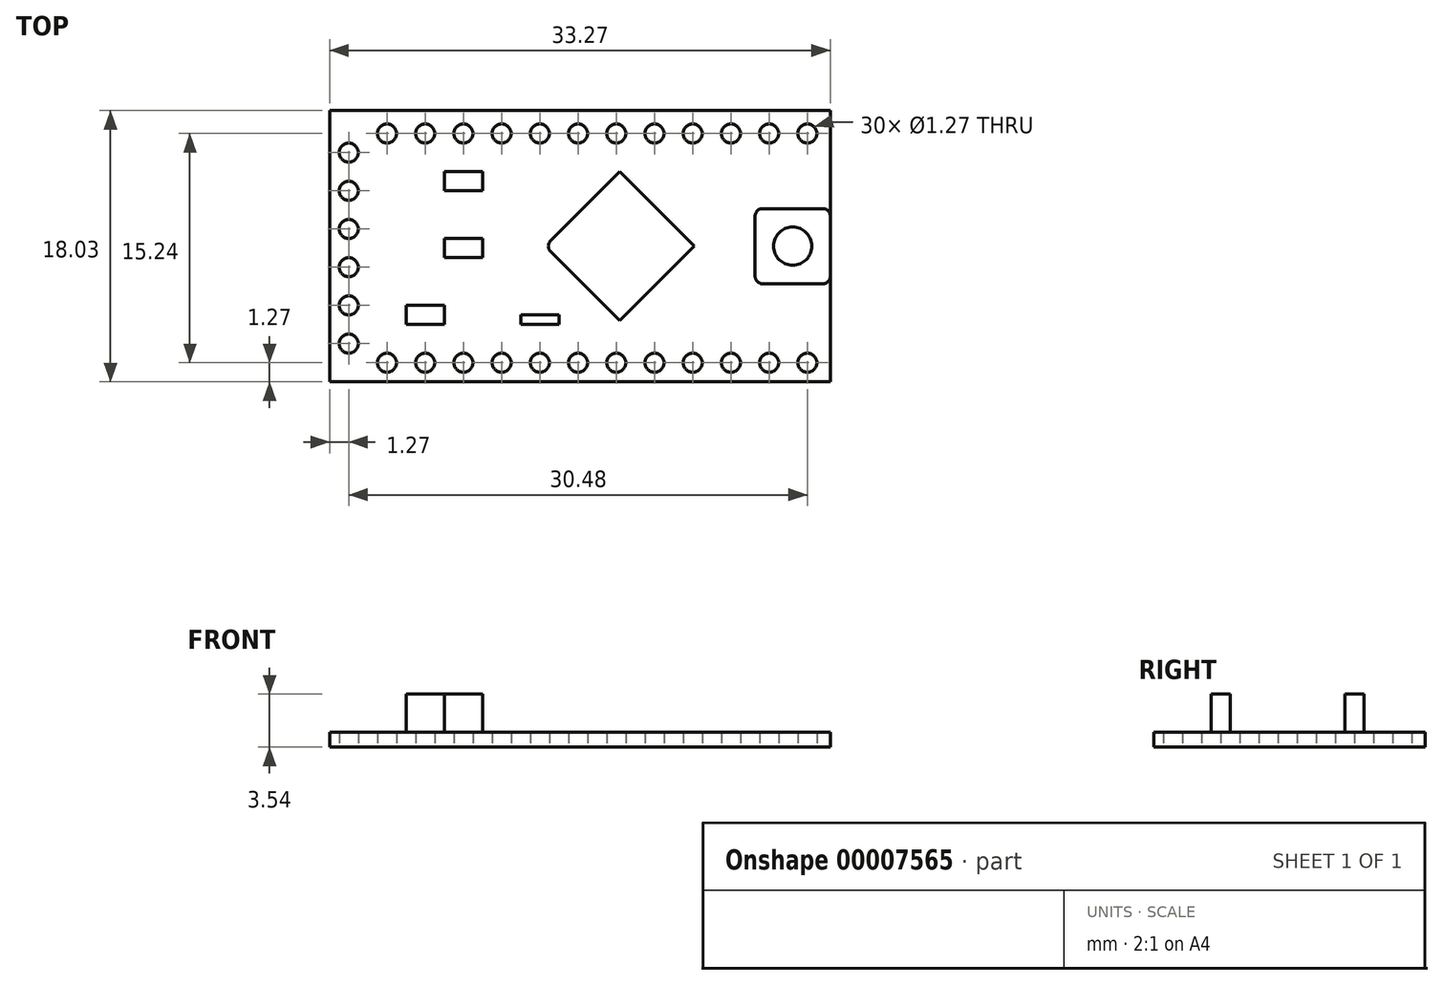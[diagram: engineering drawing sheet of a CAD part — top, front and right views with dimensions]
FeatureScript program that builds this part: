
annotation { "Feature Type Name" : "Feature", "Feature Type Description" : "" }
export const myFeature = defineFeature(function(context is Context, id is Id, definition is map)
    precondition{}
    {
        {
            var Q0;
            Q0=qCreatedBy(makeId("Top.planeOp"),FACE);
            var sketch = newSketch(context, id + "F0", { "sketchPlane" : qUnion([Q0])});
            skLineSegment(sketch, "E0.bottom", {"start": v(0, 0) * mm, "end": v(33.27, 0) * mm});
            skLineSegment(sketch, "E0.top", {"start": v(0, 18.03) * mm, "end": v(33.27, 18.03) * mm});
            skLineSegment(sketch, "E0.left", {"start": v(0, 0) * mm, "end": v(0, 18.03) * mm});
            skLineSegment(sketch, "E0.right", {"start": v(33.27, 0) * mm, "end": v(33.27, 18.03) * mm});
            skCircle(sketch, "E1", {"center": v(31.75, 16.51) * mm, "radius": 0.64 * mm});
            skCircle(sketch, "E2.1.0.0", {"center": v(29.21, 16.51) * mm, "radius": 0.64 * mm});
            skCircle(sketch, "E2.2.0.0", {"center": v(26.67, 16.51) * mm, "radius": 0.64 * mm});
            skCircle(sketch, "E2.3.0.0", {"center": v(24.13, 16.51) * mm, "radius": 0.64 * mm});
            skCircle(sketch, "E2.4.0.0", {"center": v(21.6, 16.51) * mm, "radius": 0.64 * mm});
            skCircle(sketch, "E2.5.0.0", {"center": v(19.05, 16.51) * mm, "radius": 0.64 * mm});
            skCircle(sketch, "E2.6.0.0", {"center": v(16.51, 16.51) * mm, "radius": 0.64 * mm});
            skCircle(sketch, "E2.7.0.0", {"center": v(13.97, 16.51) * mm, "radius": 0.64 * mm});
            skCircle(sketch, "E2.8.0.0", {"center": v(11.43, 16.51) * mm, "radius": 0.64 * mm});
            skCircle(sketch, "E2.9.0.0", {"center": v(8.9, 16.51) * mm, "radius": 0.64 * mm});
            skCircle(sketch, "E2.10.0.0", {"center": v(6.35, 16.51) * mm, "radius": 0.64 * mm});
            skCircle(sketch, "E2.11.0.0", {"center": v(3.8, 16.51) * mm, "radius": 0.64 * mm});
            skLineSegment(sketch, "E2.direction1", {"start": v(31.75, 16.51) * mm, "end": v(29.21, 16.51) * mm, "construction": true});
            skCircle(sketch, "E3.0.1.0", {"center": v(31.75, 1.27) * mm, "radius": 0.64 * mm});
            skCircle(sketch, "E3.0.1.1", {"center": v(26.67, 1.27) * mm, "radius": 0.64 * mm});
            skCircle(sketch, "E3.0.1.2", {"center": v(29.21, 1.27) * mm, "radius": 0.64 * mm});
            skCircle(sketch, "E3.0.1.3", {"center": v(21.6, 1.27) * mm, "radius": 0.64 * mm});
            skCircle(sketch, "E3.0.1.4", {"center": v(24.13, 1.27) * mm, "radius": 0.64 * mm});
            skCircle(sketch, "E3.0.1.5", {"center": v(16.51, 1.27) * mm, "radius": 0.64 * mm});
            skCircle(sketch, "E3.0.1.6", {"center": v(19.05, 1.27) * mm, "radius": 0.64 * mm});
            skCircle(sketch, "E3.0.1.7", {"center": v(11.43, 1.27) * mm, "radius": 0.64 * mm});
            skCircle(sketch, "E3.0.1.8", {"center": v(13.97, 1.27) * mm, "radius": 0.64 * mm});
            skCircle(sketch, "E3.0.1.9", {"center": v(6.35, 1.27) * mm, "radius": 0.64 * mm});
            skCircle(sketch, "E3.0.1.10", {"center": v(3.81, 1.27) * mm, "radius": 0.64 * mm});
            skCircle(sketch, "E3.0.1.11", {"center": v(8.9, 1.27) * mm, "radius": 0.64 * mm});
            skLineSegment(sketch, "E3.0.1.12", {"start": v(31.75, 1.27) * mm, "end": v(29.21, 1.27) * mm, "construction": true});
            skLineSegment(sketch, "E3.direction1", {"start": v(31.75, 16.51) * mm, "end": v(56.75, 16.51) * mm, "construction": true});
            skLineSegment(sketch, "E3.direction2", {"start": v(31.75, 16.51) * mm, "end": v(31.75, 1.27) * mm, "construction": true});
            skCircle(sketch, "E4", {"center": v(1.27, 2.54) * mm, "radius": 0.64 * mm});
            skCircle(sketch, "E5.0.1.0", {"center": v(1.27, 5.08) * mm, "radius": 0.64 * mm});
            skCircle(sketch, "E5.0.2.0", {"center": v(1.27, 7.62) * mm, "radius": 0.64 * mm});
            skCircle(sketch, "E5.0.3.0", {"center": v(1.27, 10.16) * mm, "radius": 0.64 * mm});
            skCircle(sketch, "E5.0.4.0", {"center": v(1.27, 12.7) * mm, "radius": 0.64 * mm});
            skCircle(sketch, "E5.0.5.0", {"center": v(1.27, 15.24) * mm, "radius": 0.64 * mm});
            skLineSegment(sketch, "E5.direction1", {"start": v(1.27, 2.54) * mm, "end": v(26.62, 2.54) * mm, "construction": true});
            skLineSegment(sketch, "E5.direction2", {"start": v(1.27, 2.54) * mm, "end": v(1.27, 5.08) * mm, "construction": true});
            skCircle(sketch, "E6.cCircle", {"center": v(19.27, 9.02) * mm, "radius": 3.5 * mm, "construction": true});
            skLineSegment(sketch, "E6.0", {"start": v(24.22, 9.02) * mm, "end": v(19.27, 4.07) * mm});
            skLineSegment(sketch, "E6.1", {"start": v(19.27, 4.07) * mm, "end": v(14.68, 8.66) * mm});
            skLineSegment(sketch, "E6.2", {"start": v(14.68, 9.37) * mm, "end": v(19.27, 13.97) * mm});
            skLineSegment(sketch, "E6.3", {"start": v(19.27, 13.97) * mm, "end": v(24.22, 9.02) * mm});
            skPoint(sketch, "E6.0.midPoint", {"position": v(21.75, 6.54) * mm});
            skLineSegment(sketch, "E7", {"start": v(0, 9.02) * mm, "end": v(33.27, 9.02) * mm, "construction": true});
            skPoint(sketch, "E8.visualSharp", {"position": v(14.32, 9.02) * mm});
            skArc(sketch, "E8.filletArc", {"start": v(14.68, 9.37) * mm, "mid": v(14.53, 9.02) * mm, "end": v(14.68, 8.66) * mm});
            skLineSegment(sketch, "E9.bottom", {"start": v(28.77, 11.52) * mm, "end": v(32.77, 11.52) * mm});
            skLineSegment(sketch, "E9.top", {"start": v(28.77, 6.52) * mm, "end": v(32.77, 6.52) * mm});
            skLineSegment(sketch, "E9.left", {"start": v(28.27, 11.02) * mm, "end": v(28.27, 7.02) * mm});
            skLineSegment(sketch, "E9.right", {"start": v(33.27, 11.02) * mm, "end": v(33.27, 7.02) * mm});
            skPoint(sketch, "E10.visualSharp", {"position": v(28.27, 11.52) * mm});
            skArc(sketch, "E10.filletArc", {"start": v(28.77, 11.52) * mm, "mid": v(28.42, 11.37) * mm, "end": v(28.27, 11.02) * mm});
            skPoint(sketch, "E11.visualSharp", {"position": v(33.27, 11.52) * mm});
            skArc(sketch, "E11.filletArc", {"start": v(33.27, 11.02) * mm, "mid": v(33.13, 11.37) * mm, "end": v(32.77, 11.52) * mm});
            skPoint(sketch, "E12.visualSharp", {"position": v(33.27, 6.52) * mm});
            skArc(sketch, "E12.filletArc", {"start": v(32.77, 6.52) * mm, "mid": v(33.13, 6.66) * mm, "end": v(33.27, 7.02) * mm});
            skPoint(sketch, "E13.visualSharp", {"position": v(28.27, 6.52) * mm});
            skArc(sketch, "E13.filletArc", {"start": v(28.27, 7.02) * mm, "mid": v(28.42, 6.66) * mm, "end": v(28.77, 6.52) * mm});
            skLineSegment(sketch, "E14.bottom", {"start": v(5.08, 5.08) * mm, "end": v(7.62, 5.08) * mm});
            skLineSegment(sketch, "E14.top", {"start": v(5.08, 3.81) * mm, "end": v(7.62, 3.81) * mm});
            skLineSegment(sketch, "E14.left", {"start": v(5.08, 5.08) * mm, "end": v(5.08, 3.81) * mm});
            skLineSegment(sketch, "E14.right", {"start": v(7.62, 5.08) * mm, "end": v(7.62, 3.81) * mm});
            skLineSegment(sketch, "E15.bottom", {"start": v(7.62, 8.26) * mm, "end": v(10.16, 8.26) * mm});
            skLineSegment(sketch, "E15.top", {"start": v(7.62, 9.53) * mm, "end": v(10.16, 9.53) * mm});
            skLineSegment(sketch, "E15.left", {"start": v(7.62, 8.26) * mm, "end": v(7.62, 9.53) * mm});
            skLineSegment(sketch, "E15.right", {"start": v(10.16, 8.26) * mm, "end": v(10.16, 9.53) * mm});
            skLineSegment(sketch, "E16.bottom", {"start": v(7.62, 12.7) * mm, "end": v(10.16, 12.7) * mm});
            skLineSegment(sketch, "E16.top", {"start": v(7.62, 13.97) * mm, "end": v(10.16, 13.97) * mm});
            skLineSegment(sketch, "E16.left", {"start": v(7.62, 12.7) * mm, "end": v(7.62, 13.97) * mm});
            skLineSegment(sketch, "E16.right", {"start": v(10.16, 12.7) * mm, "end": v(10.16, 13.97) * mm});
            skLineSegment(sketch, "E17.bottom", {"start": v(12.7, 4.45) * mm, "end": v(15.24, 4.45) * mm});
            skLineSegment(sketch, "E17.top", {"start": v(12.7, 3.81) * mm, "end": v(15.24, 3.81) * mm});
            skLineSegment(sketch, "E17.left", {"start": v(12.7, 4.45) * mm, "end": v(12.7, 3.81) * mm});
            skLineSegment(sketch, "E17.right", {"start": v(15.24, 4.45) * mm, "end": v(15.24, 3.81) * mm});
            skSolve(sketch);
        }
        {
            var Q0;
            {var subQ3=sQuery(id+"F0.wireOp",EDGE,"E0.bottom");Q0=makeQuery(id+"F0.imprint","IMPRINT",FACE,{"disambiguationData":[TD([[makeQuery(id+"F0.imprint","IMPRINT",EDGE,{"derivedFrom":subQ3}),1.0]])]});}
            var Q1;
            Q1=makeQuery(id+"F0.imprint","IMPRINT",FACE,{"disambiguationData":[TD([[makeQuery(id+"F0.imprint","IMPRINT",EDGE,{"derivedFrom":sQuery(id+"F0.wireOp",EDGE,"E6.0")}),-1.0]])]});
            var Q2;
            Q2=makeQuery(id+"F0.imprint","IMPRINT",FACE,{"disambiguationData":[TD([[makeQuery(id+"F0.imprint","IMPRINT",EDGE,{"derivedFrom":sQuery(id+"F0.wireOp",EDGE,"E9.bottom")}),-1.0]])]});
            var Q3;
            Q3=makeQuery(id+"F0.imprint","IMPRINT",FACE,{"disambiguationData":[TD([[makeQuery(id+"F0.imprint","IMPRINT",EDGE,{"derivedFrom":sQuery(id+"F0.wireOp",EDGE,"E17.bottom")}),-1.0]])]});
            var Q4;
            Q4=makeQuery(id+"F0.imprint","IMPRINT",FACE,{"disambiguationData":[TD([[makeQuery(id+"F0.imprint","IMPRINT",EDGE,{"derivedFrom":sQuery(id+"F0.wireOp",EDGE,"E14.bottom")}),-1.0]])]});
            var Q5;
            Q5=makeQuery(id+"F0.imprint","IMPRINT",FACE,{"disambiguationData":[TD([[makeQuery(id+"F0.imprint","IMPRINT",EDGE,{"derivedFrom":sQuery(id+"F0.wireOp",EDGE,"E15.bottom")}),1.0]])]});
            var Q6;
            Q6=makeQuery(id+"F0.imprint","IMPRINT",FACE,{"disambiguationData":[TD([[makeQuery(id+"F0.imprint","IMPRINT",EDGE,{"derivedFrom":sQuery(id+"F0.wireOp",EDGE,"E16.bottom")}),1.0]])]});
            extrude(context, id + "F1", {"entities" : qUnion([Q0, Q1, Q2, Q3, Q4, Q5, Q6]), "depth" : 1 * mm});
        }
        {
            var Q0;
            Q0=makeQuery(id+"F1.opExtrude","CAP_FACE",FACE,{"disambiguationData":[OSD([sQuery(id+"F0.wireOp",EDGE,"E0.bottom"),sQuery(id+"F0.wireOp",EDGE,"E0.top"),sQuery(id+"F0.wireOp",EDGE,"E0.left"),sQuery(id+"F0.wireOp",EDGE,"E0.right"),sQuery(id+"F0.wireOp",EDGE,"E1"),sQuery(id+"F0.wireOp",EDGE,"E2.1.0.0"),sQuery(id+"F0.wireOp",EDGE,"E2.2.0.0"),sQuery(id+"F0.wireOp",EDGE,"E2.3.0.0"),sQuery(id+"F0.wireOp",EDGE,"E2.4.0.0"),sQuery(id+"F0.wireOp",EDGE,"E2.5.0.0"),sQuery(id+"F0.wireOp",EDGE,"E2.6.0.0"),sQuery(id+"F0.wireOp",EDGE,"E2.7.0.0"),sQuery(id+"F0.wireOp",EDGE,"E2.8.0.0"),sQuery(id+"F0.wireOp",EDGE,"E2.9.0.0"),sQuery(id+"F0.wireOp",EDGE,"E2.10.0.0"),sQuery(id+"F0.wireOp",EDGE,"E2.11.0.0"),sQuery(id+"F0.wireOp",EDGE,"E3.0.1.0"),sQuery(id+"F0.wireOp",EDGE,"E3.0.1.1"),sQuery(id+"F0.wireOp",EDGE,"E3.0.1.2"),sQuery(id+"F0.wireOp",EDGE,"E3.0.1.3"),sQuery(id+"F0.wireOp",EDGE,"E3.0.1.4"),sQuery(id+"F0.wireOp",EDGE,"E3.0.1.5"),sQuery(id+"F0.wireOp",EDGE,"E3.0.1.6"),sQuery(id+"F0.wireOp",EDGE,"E3.0.1.7"),sQuery(id+"F0.wireOp",EDGE,"E3.0.1.8"),sQuery(id+"F0.wireOp",EDGE,"E3.0.1.9"),sQuery(id+"F0.wireOp",EDGE,"E3.0.1.10"),sQuery(id+"F0.wireOp",EDGE,"E3.0.1.11"),sQuery(id+"F0.wireOp",EDGE,"E4"),sQuery(id+"F0.wireOp",EDGE,"E5.0.1.0"),sQuery(id+"F0.wireOp",EDGE,"E5.0.2.0"),sQuery(id+"F0.wireOp",EDGE,"E5.0.3.0"),sQuery(id+"F0.wireOp",EDGE,"E5.0.4.0"),sQuery(id+"F0.wireOp",EDGE,"E5.0.5.0"),sQuery(id+"F0.wireOp",EDGE,"E9.right")])],"isStart":false});
            var sketch = newSketch(context, id + "F2", { "sketchPlane" : qUnion([Q0])});
            skLineSegment(sketch, "E18.0", {"start": v(7.62, 5.08) * mm, "end": v(7.62, 3.81) * mm});
            skLineSegment(sketch, "E19.0", {"start": v(5.08, 5.08) * mm, "end": v(7.62, 5.08) * mm});
            skLineSegment(sketch, "E20.0", {"start": v(5.08, 5.08) * mm, "end": v(5.08, 3.81) * mm});
            skLineSegment(sketch, "E21.0", {"start": v(5.08, 3.81) * mm, "end": v(7.62, 3.81) * mm});
            skLineSegment(sketch, "E22.0", {"start": v(7.62, 8.26) * mm, "end": v(10.16, 8.26) * mm});
            skLineSegment(sketch, "E23.0", {"start": v(7.62, 8.26) * mm, "end": v(7.62, 9.53) * mm});
            skLineSegment(sketch, "E23.2", {"start": v(10.16, 8.26) * mm, "end": v(10.16, 9.53) * mm});
            skLineSegment(sketch, "E24.0", {"start": v(7.62, 9.53) * mm, "end": v(10.16, 9.53) * mm});
            skLineSegment(sketch, "E25.0", {"start": v(7.62, 12.7) * mm, "end": v(10.16, 12.7) * mm});
            skLineSegment(sketch, "E26.0", {"start": v(7.62, 12.7) * mm, "end": v(7.62, 13.97) * mm});
            skLineSegment(sketch, "E27.0", {"start": v(7.62, 13.97) * mm, "end": v(10.16, 13.97) * mm});
            skLineSegment(sketch, "E28.0", {"start": v(10.16, 12.7) * mm, "end": v(10.16, 13.97) * mm});
            skLineSegment(sketch, "E29.0", {"start": v(12.7, 4.45) * mm, "end": v(15.24, 4.45) * mm});
            skLineSegment(sketch, "E30.0", {"start": v(12.7, 3.81) * mm, "end": v(15.24, 3.81) * mm});
            skLineSegment(sketch, "E31.0", {"start": v(12.7, 4.45) * mm, "end": v(12.7, 3.81) * mm});
            skLineSegment(sketch, "E32.0", {"start": v(15.24, 4.45) * mm, "end": v(15.24, 3.81) * mm});
            skLineSegment(sketch, "E33.0", {"start": v(14.68, 9.37) * mm, "end": v(19.27, 13.97) * mm});
            skLineSegment(sketch, "E33.1", {"start": v(19.27, 13.97) * mm, "end": v(24.22, 9.02) * mm});
            skLineSegment(sketch, "E33.2", {"start": v(24.22, 9.02) * mm, "end": v(19.27, 4.07) * mm});
            skLineSegment(sketch, "E33.3", {"start": v(19.27, 4.07) * mm, "end": v(14.68, 8.66) * mm});
            skArc(sketch, "E33.4", {"start": v(14.68, 9.37) * mm, "mid": v(14.53, 9.02) * mm, "end": v(14.68, 8.66) * mm});
            skLineSegment(sketch, "E33.5", {"start": v(28.27, 11.02) * mm, "end": v(28.27, 7.02) * mm});
            skLineSegment(sketch, "E33.6", {"start": v(28.77, 6.52) * mm, "end": v(32.77, 6.52) * mm});
            skLineSegment(sketch, "E33.7", {"start": v(28.77, 11.52) * mm, "end": v(32.77, 11.52) * mm});
            skLineSegment(sketch, "E33.8", {"start": v(33.27, 11.02) * mm, "end": v(33.27, 7.02) * mm});
            skArc(sketch, "E33.9", {"start": v(33.27, 11.02) * mm, "mid": v(33.13, 11.37) * mm, "end": v(32.77, 11.52) * mm});
            skArc(sketch, "E33.10", {"start": v(28.77, 11.52) * mm, "mid": v(28.42, 11.37) * mm, "end": v(28.27, 11.02) * mm});
            skArc(sketch, "E33.11", {"start": v(28.27, 7.02) * mm, "mid": v(28.42, 6.66) * mm, "end": v(28.77, 6.52) * mm});
            skArc(sketch, "E33.12", {"start": v(32.77, 6.52) * mm, "mid": v(33.13, 6.66) * mm, "end": v(33.27, 7.02) * mm});
            skSolve(sketch);
        }
        {
            var Q0;
            Q0=makeQuery(id+"F2.imprint","IMPRINT",FACE,{"disambiguationData":[TD([[makeQuery(id+"F2.imprint","IMPRINT",EDGE,{"derivedFrom":sQuery(id+"F2.wireOp",EDGE,"E18.0")}),-1.0]])]});
            var Q1;
            Q1=makeQuery(id+"F2.imprint","IMPRINT",FACE,{"disambiguationData":[TD([[makeQuery(id+"F2.imprint","IMPRINT",EDGE,{"derivedFrom":sQuery(id+"F2.wireOp",EDGE,"E25.0")}),1.0]])]});
            extrude(context, id + "F3", {"entities" : qUnion([Q0, Q1]), "operationType" : NewBodyOperationType.ADD, "depth" : 2.54 * mm});
        }
        {
            var Q0;
            Q0=makeQuery(id+"F2.imprint","IMPRINT",FACE,{"disambiguationData":[TD([[makeQuery(id+"F2.imprint","IMPRINT",EDGE,{"derivedFrom":sQuery(id+"F2.wireOp",EDGE,"E23.0")}),-1.0]])]});
            extrude(context, id + "F4", {"entities" : qUnion([Q0]), "operationType" : NewBodyOperationType.ADD, "depth" : .1 / 50.8 * mm});
        }
        {
            var Q0;
            Q0=makeQuery(id+"F2.imprint","IMPRINT",FACE,{"disambiguationData":[TD([[makeQuery(id+"F2.imprint","IMPRINT",EDGE,{"derivedFrom":sQuery(id+"F2.wireOp",EDGE,"E33.0")}),-1.0]])]});
            var Q1;
            Q1=makeQuery(id+"F2.imprint","IMPRINT",FACE,{"disambiguationData":[TD([[makeQuery(id+"F2.imprint","IMPRINT",EDGE,{"derivedFrom":sQuery(id+"F2.wireOp",EDGE,"E33.5")}),1.0]])]});
            var Q2;
            Q2=makeQuery(id+"F2.imprint","IMPRINT",FACE,{"disambiguationData":[TD([[makeQuery(id+"F2.imprint","IMPRINT",EDGE,{"derivedFrom":sQuery(id+"F2.wireOp",EDGE,"E29.0")}),-1.0]])]});
            extrude(context, id + "F5", {"entities" : qUnion([Q0, Q1, Q2]), "operationType" : NewBodyOperationType.ADD, "depth" : .1 / 50.8 * mm});
        }
        {
            var Q0;
            Q0=makeQuery(id+"F5.opExtrude","CAP_FACE",FACE,{"disambiguationData":[OSD([sQuery(id+"F2.wireOp",EDGE,"E33.5"),sQuery(id+"F2.wireOp",EDGE,"E33.6"),sQuery(id+"F2.wireOp",EDGE,"E33.7"),sQuery(id+"F2.wireOp",EDGE,"E33.8"),sQuery(id+"F2.wireOp",EDGE,"E33.9"),sQuery(id+"F2.wireOp",EDGE,"E33.10"),sQuery(id+"F2.wireOp",EDGE,"E33.11"),sQuery(id+"F2.wireOp",EDGE,"E33.12")])],"isStart":false});
            var sketch = newSketch(context, id + "F6", { "sketchPlane" : qUnion([Q0])});
            skCircle(sketch, "E34", {"center": v(30.77, 9.02) * mm, "radius": 1.27 * mm});
            skLineSegment(sketch, "E35", {"start": v(28.27, 9.02) * mm, "end": v(33.27, 9.02) * mm, "construction": true});
            skLineSegment(sketch, "E36", {"start": v(30.77, 11.52) * mm, "end": v(30.77, 6.52) * mm, "construction": true});
            skSolve(sketch);
        }
        {
            var Q0;
            Q0=makeQuery(id+"F6.imprint","IMPRINT",FACE,{"disambiguationData":[TD([[makeQuery(id+"F6.imprint","IMPRINT",EDGE,{"derivedFrom":sQuery(id+"F6.wireOp",EDGE,"E34")}),1.0]])]});
            extrude(context, id + "F7", {"entities" : qUnion([Q0]), "operationType" : NewBodyOperationType.ADD, "depth" : .1 / 101.6 * mm});
        }
    });
